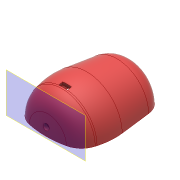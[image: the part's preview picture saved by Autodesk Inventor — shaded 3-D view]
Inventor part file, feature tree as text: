
AUTODESK INVENTOR PART (.ipt)
format: ipt  version: 2017 (Build 210142000, 142)  size: 258,048 bytes
history: native  units: mm
features: sketch x8, extrude x6, fillet x4, projected_geometry x2, revolve x1, chamfer x1, shell x1, hole x1, plane x1
ambient origin geometry x8: Origin, YZ Plane, XZ Plane, XY Plane, X Axis, Y Axis, Z Axis, Center Point
bodies: Solid1 (feature_tree)
feature tree (25):
  revolve  "Revolution1"  [1 undecoded]
  fillet  "Fillet1"  Radius=30.0mm
  chamfer  "Chamfer1"  Distance=10.0mm Angle=45.0deg
  fillet  "Fillet2"  Radius=20.0mm
  fillet  "Fillet3"  Radius=60.0mm
  extrude  "Extrusion1"  Depth=4.0mm
  shell  "Shell1"  Thickness=100.0mm
  extrude  "Extrusion3"  Depth=12.0mm
  extrude  "Extrusion4"  Depth=8.0mm
  hole  "Hole1"  [1 undecoded]
  plane  "Work Plane1"
  extrude  "Extrusion5"  [1 undecoded]
  fillet  "Fillet4"  Radius=6.0mm
  extrude  "Extrusion6"  Depth=4.0mm TaperAngle=0.0deg
  extrude  "Extrusion7"  Depth=9.0mm
  sketch  "Sketch1"  dims[d0=40.0mm d1=80.0mm d2=30.0mm]
  sketch  "Sketch2"  dims[d3=90.0deg]
  sketch  "Sketch4"  dims[d4=20.0mm d5=10.0mm d6=20.0mm d7=45.0deg d8=20.0mm d9=60.0mm]
  sketch  "Sketch5"  dims[d10=10.0mm d11=0.0mm d12=4.0mm d18=100.0mm d20=80.0mm]
  sketch  "Sketch6"  dims[d32=6.0mm d33=12.0mm]
  projected_geometry  "Projected Loop1"
  sketch  "Sketch7"  dims[d34=14.0mm d35=0.0mm d36=8.0mm]
  sketch  "Sketch8"  dims[d37=24.0mm d38=4.0mm d39=0.0mm]
  sketch  "Sketch9"  dims[d40=8.0mm d41=3.5mm d42=6.0mm d43=4.0mm d44=2.0mm d45=90.0deg d46=8.0mm d47=20.594885mm d48=-9.5mm d49=6.0mm d50=4.0mm d51=0.0mm d52=2.0mm d53=20.0mm d54=6.0mm d55=10.0mm d56=32.0mm d57=0.0mm d58=4.0mm d59=1.0mm d60=10.0mm d61=9.0mm d62=32.0mm d63=0.0mm]
  projected_geometry  "Projected Loop2"
note: 3 required parameter values undecoded (feature->parameter linkage not recoverable at this tier; creation-order binding heuristic only, values carry confidence <= 0.55)